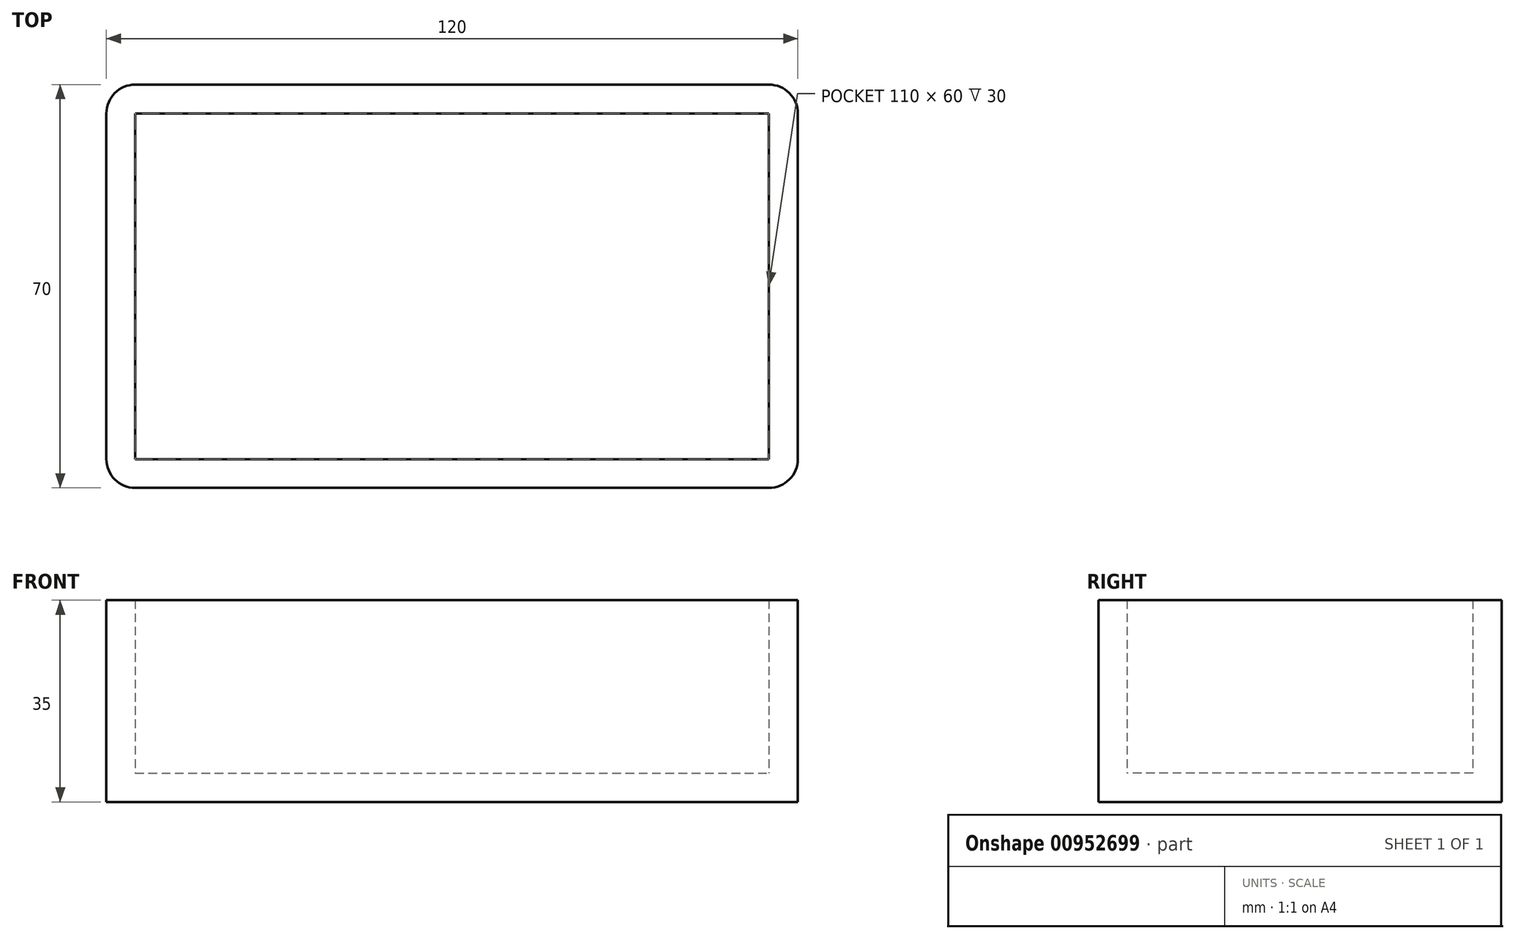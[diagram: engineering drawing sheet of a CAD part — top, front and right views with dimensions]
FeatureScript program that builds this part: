
annotation { "Feature Type Name" : "Feature", "Feature Type Description" : "" }
export const myFeature = defineFeature(function(context is Context, id is Id, definition is map)
    precondition{}
    {
        {
            var Q0;
            Q0=qCreatedBy(makeId("Top.planeOp"),FACE);
            var sketch = newSketch(context, id + "F0", { "sketchPlane" : qUnion([Q0])});
            skLineSegment(sketch, "E0.bottom", {"start": v(-55, 35) * mm, "end": v(55, 35) * mm});
            skLineSegment(sketch, "E0.top", {"start": v(-55, -35) * mm, "end": v(55, -35) * mm});
            skLineSegment(sketch, "E0.left", {"start": v(-60, 30) * mm, "end": v(-60, -30) * mm});
            skLineSegment(sketch, "E0.right", {"start": v(60, 30) * mm, "end": v(60, -30) * mm});
            skPoint(sketch, "E0.middle", {"position": v(0, 0) * mm});
            skPoint(sketch, "E1.visualSharp", {"position": v(-60, 35) * mm});
            skArc(sketch, "E1.filletArc", {"start": v(-55, 35) * mm, "mid": v(-58.54, 33.54) * mm, "end": v(-60, 30) * mm});
            skPoint(sketch, "E2.visualSharp", {"position": v(-60, -35) * mm});
            skArc(sketch, "E2.filletArc", {"start": v(-60, -30) * mm, "mid": v(-58.54, -33.54) * mm, "end": v(-55, -35) * mm});
            skPoint(sketch, "E3.visualSharp", {"position": v(60, -35) * mm});
            skArc(sketch, "E3.filletArc", {"start": v(55, -35) * mm, "mid": v(58.54, -33.54) * mm, "end": v(60, -30) * mm});
            skPoint(sketch, "E4.visualSharp", {"position": v(60, 35) * mm});
            skArc(sketch, "E4.filletArc", {"start": v(60, 30) * mm, "mid": v(58.54, 33.54) * mm, "end": v(55, 35) * mm});
            skSolve(sketch);
        }
        {
            var Q0;
            Q0=makeQuery(id+"F0.imprint","IMPRINT",FACE,{"disambiguationData":[TD([[makeQuery(id+"F0.imprint","IMPRINT",EDGE,{"derivedFrom":sQuery(id+"F0.wireOp",EDGE,"E0.bottom")}),-1.0]])]});
            extrude(context, id + "F1", {"entities" : qUnion([Q0]), "depth" : 35 * mm, "offsetDistance" : 25 * mm});
        }
        {
            var Q0;
            Q0=makeQuery(id+"F1.opExtrude","CAP_FACE",FACE,{"disambiguationData":[OSD([sQuery(id+"F0.wireOp",EDGE,"E0.bottom"),sQuery(id+"F0.wireOp",EDGE,"E0.top"),sQuery(id+"F0.wireOp",EDGE,"E0.left"),sQuery(id+"F0.wireOp",EDGE,"E0.right"),sQuery(id+"F0.wireOp",EDGE,"E1.filletArc"),sQuery(id+"F0.wireOp",EDGE,"E2.filletArc"),sQuery(id+"F0.wireOp",EDGE,"E3.filletArc"),sQuery(id+"F0.wireOp",EDGE,"E4.filletArc")])],"isStart":false});
            shell(context, id + "F2", {"entities" : qUnion([Q0]), "thickness" : 5 * mm});
        }
    });
